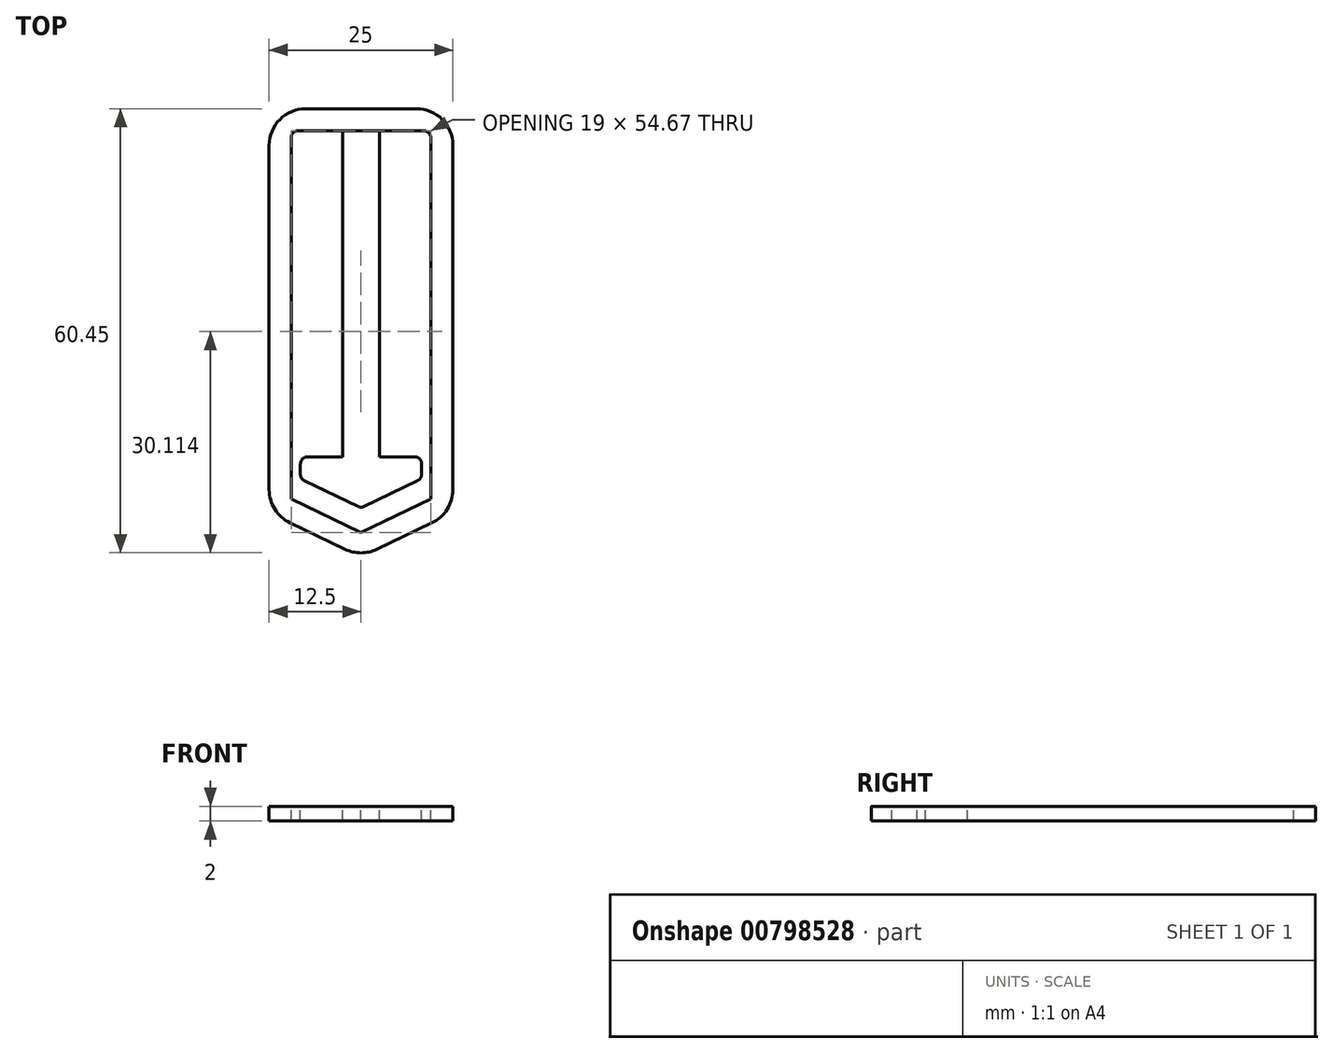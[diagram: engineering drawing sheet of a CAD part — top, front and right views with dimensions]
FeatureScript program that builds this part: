
annotation { "Feature Type Name" : "Feature", "Feature Type Description" : "" }
export const myFeature = defineFeature(function(context is Context, id is Id, definition is map)
    precondition{}
    {
        {
            var Q0;
            Q0=qCreatedBy(makeId("Top.planeOp"),FACE);
            var sketch = newSketch(context, id + "F0", { "sketchPlane" : qUnion([Q0])});
            skLineSegment(sketch, "E0", {"start": v(0, 0) * mm, "end": v(25, 0) * mm});
            skLineSegment(sketch, "E1", {"start": v(25, 0) * mm, "end": v(25, -55) * mm});
            skLineSegment(sketch, "E2", {"start": v(25, -55) * mm, "end": v(12.5, -61) * mm});
            skLineSegment(sketch, "E3", {"start": v(12.5, -61) * mm, "end": v(0, -55) * mm});
            skLineSegment(sketch, "E4", {"start": v(0, -55) * mm, "end": v(0, 0) * mm});
            skSolve(sketch);
        }
        {
            var Q0;
            Q0 = qSketchRegion(id + "F0", true);
            extrude(context, id + "F1", {"entities" : qUnion([Q0]), "depth" : 2 * mm, "offsetDistance" : 25 * mm});
        }
        {
            var Q0;
            Q0=makeQuery(id+"F1.opExtrude","CAP_FACE",FACE,{"disambiguationData":[OSD([sQuery(id+"F0.wireOp",EDGE,"E0"),sQuery(id+"F0.wireOp",EDGE,"E1"),sQuery(id+"F0.wireOp",EDGE,"E2"),sQuery(id+"F0.wireOp",EDGE,"E3"),sQuery(id+"F0.wireOp",EDGE,"E4")])],"isStart":false});
            var sketch = newSketch(context, id + "F2", { "sketchPlane" : qUnion([Q0])});
            skLineSegment(sketch, "E5.0", {"start": v(0, 0) * mm, "end": v(25, 0) * mm, "construction": true});
            skLineSegment(sketch, "E5.1", {"start": v(25, 0) * mm, "end": v(25, -55) * mm, "construction": true});
            skLineSegment(sketch, "E5.2", {"start": v(0, -55) * mm, "end": v(0, 0) * mm, "construction": true});
            skLineSegment(sketch, "E5.3", {"start": v(12.5, -61) * mm, "end": v(0, -55) * mm, "construction": true});
            skLineSegment(sketch, "E5.4", {"start": v(25, -55) * mm, "end": v(12.5, -61) * mm, "construction": true});
            skLineSegment(sketch, "E6.0", {"start": v(22, -3) * mm, "end": v(22, -53.11) * mm});
            skLineSegment(sketch, "E6.1", {"start": v(3, -3) * mm, "end": v(22, -3) * mm});
            skLineSegment(sketch, "E6.2", {"start": v(22, -53.11) * mm, "end": v(12.5, -57.67) * mm});
            skLineSegment(sketch, "E6.3", {"start": v(12.5, -57.67) * mm, "end": v(3, -53.11) * mm});
            skLineSegment(sketch, "E6.4", {"start": v(3, -53.11) * mm, "end": v(3, -3) * mm});
            skSolve(sketch);
        }
        {
            var Q0;
            Q0 = qSketchRegion(id + "F2", true);
            extrude(context, id + "F3", {"entities" : qUnion([Q0]), "operationType" : NewBodyOperationType.REMOVE, "endBound" : BoundingType.THROUGH_ALL, "oppositeDirection" : true, "depth" : 25 * mm, "offsetDistance" : 25 * mm});
        }
        {
            var Q0;
            Q0=makeQuery(id+"F1.opExtrude","CAP_FACE",FACE,{"disambiguationData":[OSD([sQuery(id+"F0.wireOp",EDGE,"E0"),sQuery(id+"F0.wireOp",EDGE,"E1"),sQuery(id+"F0.wireOp",EDGE,"E2"),sQuery(id+"F0.wireOp",EDGE,"E3"),sQuery(id+"F0.wireOp",EDGE,"E4")])],"isStart":false});
            var sketch = newSketch(context, id + "F4", { "sketchPlane" : qUnion([Q0])});
            skLineSegment(sketch, "E7.0", {"start": v(10, -3) * mm, "end": v(15, -3) * mm});
            skLineSegment(sketch, "E8.0", {"start": v(22, -53.11) * mm, "end": v(12.5, -57.67) * mm, "construction": true});
            skLineSegment(sketch, "E8.1", {"start": v(12.5, -57.67) * mm, "end": v(3, -53.11) * mm, "construction": true});
            skLineSegment(sketch, "E9.0", {"start": v(12.5, -54.34) * mm, "end": v(4.25, -50.38) * mm});
            skLineSegment(sketch, "E9.1", {"start": v(20.75, -50.38) * mm, "end": v(12.5, -54.34) * mm});
            skLineSegment(sketch, "E10", {"start": v(4.25, -50.38) * mm, "end": v(4.25, -47.38) * mm});
            skLineSegment(sketch, "E11", {"start": v(4.25, -47.38) * mm, "end": v(10, -47.38) * mm});
            skLineSegment(sketch, "E12", {"start": v(20.75, -47.38) * mm, "end": v(20.75, -50.38) * mm});
            skLineSegment(sketch, "E13", {"start": v(12.5, -54.34) * mm, "end": v(12.5, -3) * mm, "construction": true});
            skLineSegment(sketch, "E14", {"start": v(10, -47.38) * mm, "end": v(10, -3) * mm});
            skLineSegment(sketch, "E15", {"start": v(15, -47.38) * mm, "end": v(15, -3) * mm});
            skPoint(sketch, "E16.orphan", {"position": v(3, -3) * mm});
            skPoint(sketch, "E17.orphan", {"position": v(22, -3) * mm});
            skLineSegment(sketch, "E18.trimOffspring", {"start": v(15, -47.38) * mm, "end": v(20.75, -47.38) * mm});
            skSolve(sketch);
        }
        {
            var Q0;
            Q0 = qSketchRegion(id + "F4", true);
            var Q1;
            Q1=makeQuery(id+"F1.opExtrude","CAP_FACE",FACE,{"disambiguationData":[OSD([sQuery(id+"F0.wireOp",EDGE,"E0"),sQuery(id+"F0.wireOp",EDGE,"E1"),sQuery(id+"F0.wireOp",EDGE,"E2"),sQuery(id+"F0.wireOp",EDGE,"E3"),sQuery(id+"F0.wireOp",EDGE,"E4")])],"isStart":true});
            extrude(context, id + "F5", {"entities" : qUnion([Q0]), "endBound" : BoundingType.UP_TO_SURFACE, "oppositeDirection" : true, "depth" : 25 * mm, "endBoundEntityFace" : qUnion([Q1]), "offsetDistance" : 25 * mm});
        }
        {
            var Q0;
            Q0=makeQuery(id+"F1.opExtrude","SWEPT_EDGE",EDGE,{"disambiguationData":[OSD([sQuery(id+"F0.wireOp",EDGE,"E0"),sQuery(id+"F0.wireOp",EDGE,"E4")])]});
            var Q1;
            Q1=makeQuery(id+"F1.opExtrude","SWEPT_EDGE",EDGE,{"disambiguationData":[OSD([sQuery(id+"F0.wireOp",EDGE,"E0"),sQuery(id+"F0.wireOp",EDGE,"E1")])]});
            var Q2;
            Q2=makeQuery(id+"F1.opExtrude","SWEPT_EDGE",EDGE,{"disambiguationData":[OSD([sQuery(id+"F0.wireOp",EDGE,"E1"),sQuery(id+"F0.wireOp",EDGE,"E2")])]});
            var Q3;
            Q3=makeQuery(id+"F1.opExtrude","SWEPT_EDGE",EDGE,{"disambiguationData":[OSD([sQuery(id+"F0.wireOp",EDGE,"E2"),sQuery(id+"F0.wireOp",EDGE,"E3")])]});
            var Q4;
            Q4=makeQuery(id+"F1.opExtrude","SWEPT_EDGE",EDGE,{"disambiguationData":[OSD([sQuery(id+"F0.wireOp",EDGE,"E3"),sQuery(id+"F0.wireOp",EDGE,"E4")])]});
            fillet(context, id + "F6", {"entities" : qUnion([Q0, Q1, Q2, Q3, Q4]), "radius" : 5 * mm, "tangentPropagation" : true, "allowEdgeOverflow" : false});
        }
        {
            var Q0;
            Q0=makeQuery(id+"F3.boolean.opBoolean","COPY",EDGE,{"derivedFrom":makeQuery(id+"F3.opExtrude","SWEPT_EDGE",EDGE,{"disambiguationData":[OSD([sQuery(id+"F2.wireOp",EDGE,"E6.1"),sQuery(id+"F2.wireOp",EDGE,"E6.4")])]})});
            var Q1;
            Q1=makeQuery(id+"F3.boolean.opBoolean","COPY",EDGE,{"derivedFrom":makeQuery(id+"F3.opExtrude","SWEPT_EDGE",EDGE,{"disambiguationData":[OSD([sQuery(id+"F2.wireOp",EDGE,"E6.0"),sQuery(id+"F2.wireOp",EDGE,"E6.1")])]})});
            var Q2;
            Q2=makeQuery(id+"F5.opExtrude","SWEPT_EDGE",EDGE,{"disambiguationData":[OSD([sQuery(id+"F4.wireOp",EDGE,"E12"),sQuery(id+"F4.wireOp",EDGE,"E18.trimOffspring")])]});
            var Q3;
            Q3=makeQuery(id+"F5.opExtrude","SWEPT_EDGE",EDGE,{"disambiguationData":[OSD([sQuery(id+"F4.wireOp",EDGE,"E9.1"),sQuery(id+"F4.wireOp",EDGE,"E12")])]});
            var Q4;
            Q4=makeQuery(id+"F5.opExtrude","SWEPT_EDGE",EDGE,{"disambiguationData":[OSD([sQuery(id+"F4.wireOp",EDGE,"E9.0"),sQuery(id+"F4.wireOp",EDGE,"E9.1")])]});
            var Q5;
            Q5=makeQuery(id+"F5.opExtrude","SWEPT_EDGE",EDGE,{"disambiguationData":[OSD([sQuery(id+"F4.wireOp",EDGE,"E9.0"),sQuery(id+"F4.wireOp",EDGE,"E10")])]});
            var Q6;
            Q6=makeQuery(id+"F5.opExtrude","SWEPT_EDGE",EDGE,{"disambiguationData":[OSD([sQuery(id+"F4.wireOp",EDGE,"E10"),sQuery(id+"F4.wireOp",EDGE,"E11")])]});
            fillet(context, id + "F7", {"entities" : qUnion([Q0, Q1, Q2, Q3, Q4, Q5, Q6]), "radius" : 1 * mm, "tangentPropagation" : true, "allowEdgeOverflow" : false});
        }
    });
